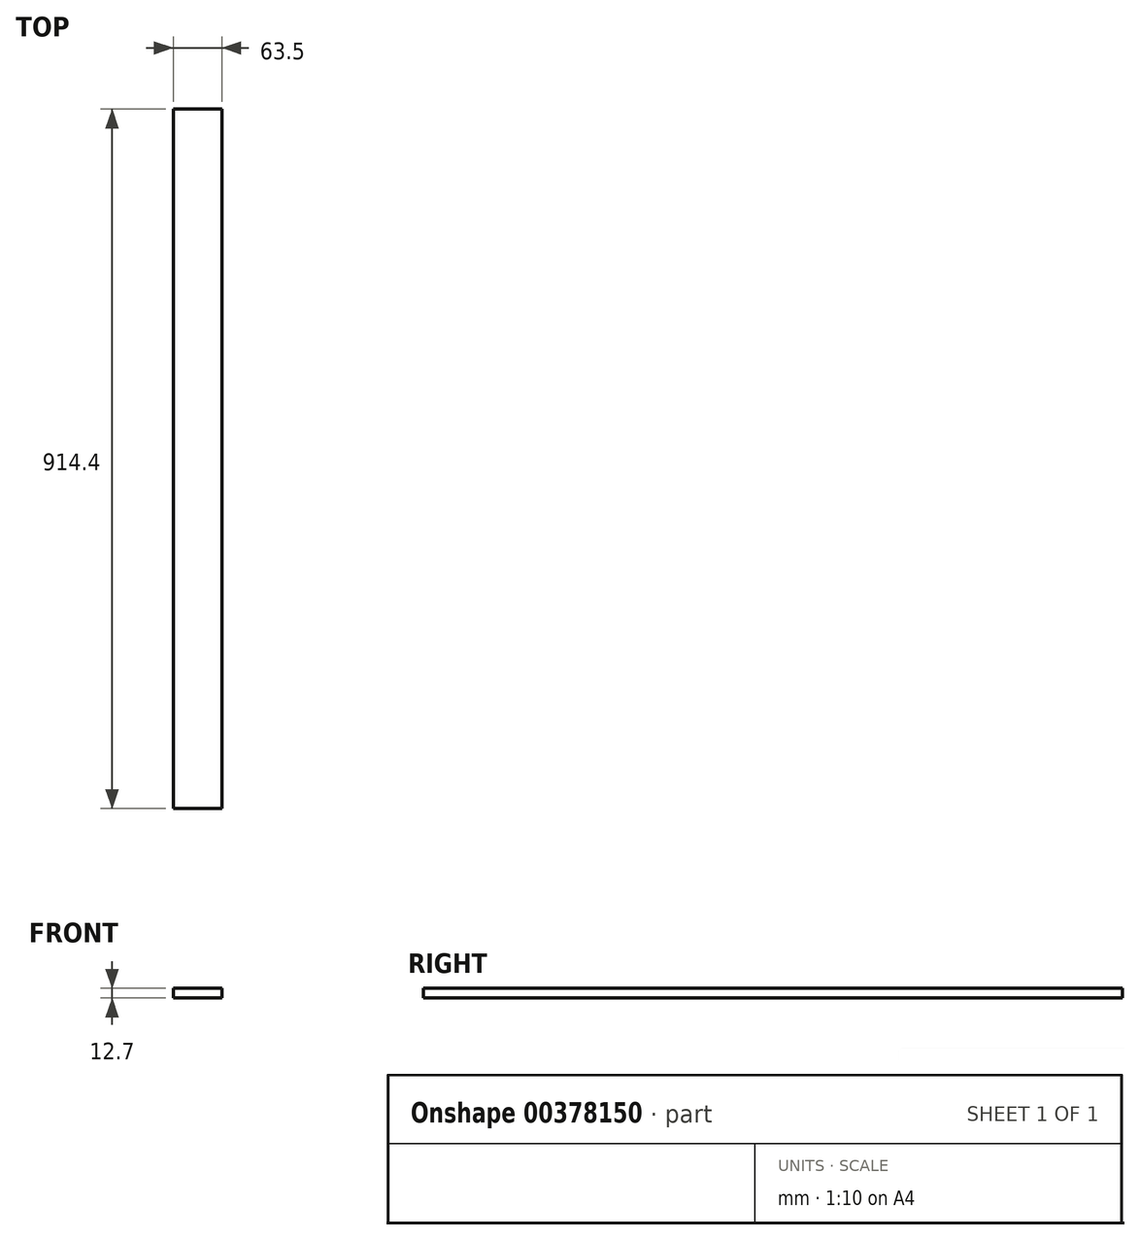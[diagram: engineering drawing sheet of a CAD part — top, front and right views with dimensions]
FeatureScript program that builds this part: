
annotation { "Feature Type Name" : "Feature", "Feature Type Description" : "" }
export const myFeature = defineFeature(function(context is Context, id is Id, definition is map)
    precondition{}
    {
        {
            var Q0;
            Q0=qCreatedBy(makeId("Front.planeOp"),FACE);
            var sketch = newSketch(context, id + "F0", { "sketchPlane" : qUnion([Q0])});
            skLineSegment(sketch, "E0.bottom", {"start": v(31.75, 6.35) * mm, "end": v(-31.75, 6.35) * mm});
            skLineSegment(sketch, "E0.top", {"start": v(31.75, -6.35) * mm, "end": v(-31.75, -6.35) * mm});
            skLineSegment(sketch, "E0.left", {"start": v(31.75, 6.35) * mm, "end": v(31.75, -6.35) * mm});
            skLineSegment(sketch, "E0.right", {"start": v(-31.75, 6.35) * mm, "end": v(-31.75, -6.35) * mm});
            skPoint(sketch, "E0.middle", {"position": v(0, 0) * mm});
            skSolve(sketch);
        }
        {
            var Q0;
            Q0=qSketchRegion(id+"F0",true);
            extrude(context, id + "F1", {"entities" : qUnion([Q0]), "endBound" : BoundingType.SYMMETRIC, "depth" : 914.4 * mm});
        }
    });
